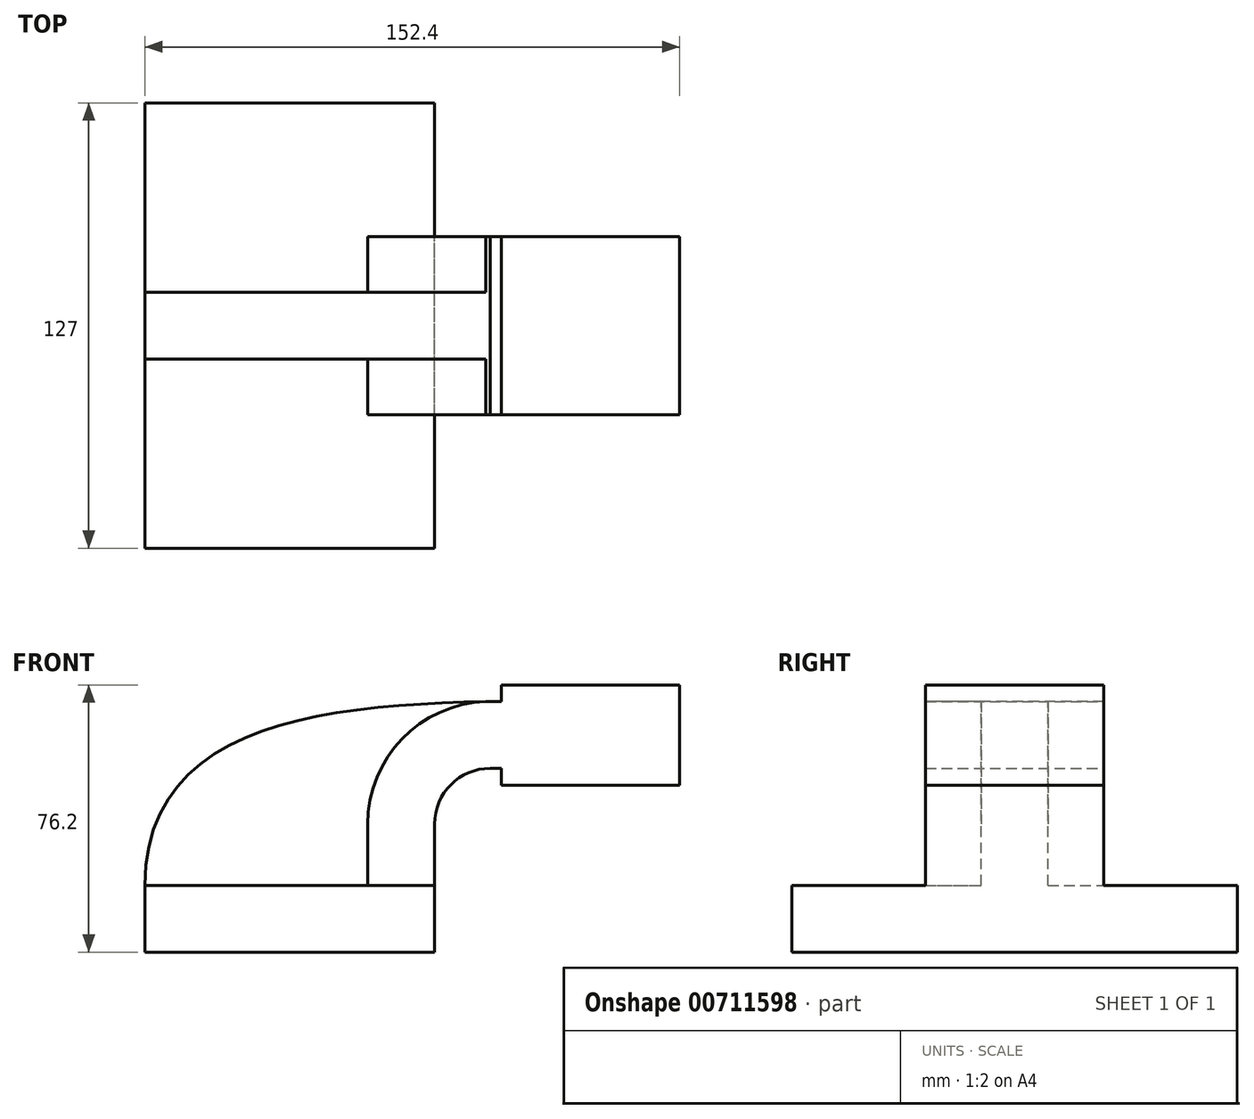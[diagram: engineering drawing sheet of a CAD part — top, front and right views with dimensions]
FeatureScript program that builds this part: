
annotation { "Feature Type Name" : "Feature", "Feature Type Description" : "" }
export const myFeature = defineFeature(function(context is Context, id is Id, definition is map)
    precondition{}
    {
        {
            var Q0;
            Q0=qCreatedBy(makeId("Front.planeOp"),FACE);
            var sketch = newSketch(context, id + "F0", { "sketchPlane" : qUnion([Q0])});
            skLineSegment(sketch, "E0.bottom", {"start": v(41.28, -9.52) * mm, "end": v(-41.28, -9.53) * mm});
            skLineSegment(sketch, "E0.top", {"start": v(41.28, 9.53) * mm, "end": v(-41.28, 9.53) * mm});
            skLineSegment(sketch, "E0.left", {"start": v(41.28, -9.52) * mm, "end": v(41.28, 9.53) * mm});
            skLineSegment(sketch, "E0.right", {"start": v(-41.28, -9.53) * mm, "end": v(-41.28, 9.53) * mm});
            skPoint(sketch, "E0.middle", {"position": v(0, 0) * mm});
            skLineSegment(sketch, "E1.bottom", {"start": v(60.33, 66.68) * mm, "end": v(111.13, 66.68) * mm});
            skLineSegment(sketch, "E1.top", {"start": v(60.33, 38.1) * mm, "end": v(111.13, 38.1) * mm});
            skLineSegment(sketch, "E1.left", {"start": v(60.33, 66.68) * mm, "end": v(60.33, 38.1) * mm});
            skLineSegment(sketch, "E1.right", {"start": v(111.13, 66.68) * mm, "end": v(111.13, 38.1) * mm});
            skPoint(sketch, "E1.middle", {"position": v(85.72, 52.39) * mm});
            skLineSegment(sketch, "E2", {"start": v(41.28, 9.53) * mm, "end": v(41.28, 27) * mm});
            skArc(sketch, "E3", {"start": v(41.27, 27) * mm, "mid": v(45.92, 38.23) * mm, "end": v(57.15, 42.88) * mm});
            skLineSegment(sketch, "E4", {"start": v(57.15, 42.88) * mm, "end": v(85.73, 42.88) * mm});
            skLineSegment(sketch, "E5.0", {"start": v(57.15, 61.93) * mm, "end": v(85.73, 61.93) * mm});
            skArc(sketch, "E5.1", {"start": v(22.23, 27) * mm, "mid": v(32.45, 51.7) * mm, "end": v(57.15, 61.93) * mm});
            skLineSegment(sketch, "E5.2", {"start": v(22.23, 9.53) * mm, "end": v(22.23, 27) * mm});
            skFitSpline(sketch, "E6", {"points": [v(-41.28, 9.53) * mm, v(57.15, 61.93) * mm], "startDerivative": vector(0.26, 138.07) * mm, "endDerivative": vector(143.87, 2.5) * mm});
            skSolve(sketch);
        }
        {
            var Q0;
            Q0=makeQuery(id+"F0.imprint","IMPRINT",FACE,{"disambiguationData":[TD([[makeQuery(id+"F0.imprint","IMPRINT",EDGE,{"derivedFrom":sQuery(id+"F0.wireOp",EDGE,"E0.bottom")}),-1.0]])]});
            extrude(context, id + "F1", {"entities" : qUnion([Q0]), "endBound" : BoundingType.SYMMETRIC, "depth" : 127 * mm, "offsetDistance" : 25.4 * mm});
        }
        {
            var Q0;
            {var subQ1=sQuery(id+"F0.wireOp",EDGE,"E2");Q0=makeQuery(id+"F0.imprint","IMPRINT",FACE,{"disambiguationData":[TD([[makeQuery(id+"F0.imprint","IMPRINT",EDGE,{"derivedFrom":subQ1}),1.0]])]});}
            var Q1;
            {var subQ3=sQuery(id+"F0.wireOp",EDGE,"E1.bottom");Q1=makeQuery(id+"F0.imprint","IMPRINT",FACE,{"disambiguationData":[TD([[makeQuery(id+"F0.imprint","IMPRINT",EDGE,{"derivedFrom":subQ3}),-1.0]])]});}
            extrude(context, id + "F2", {"entities" : qUnion([Q0, Q1]), "operationType" : NewBodyOperationType.ADD, "endBound" : BoundingType.SYMMETRIC, "depth" : 50.8 * mm, "offsetDistance" : 25.4 * mm});
        }
        {
            var Q0;
            {var subQ3=sQuery(id+"F0.wireOp",EDGE,"E5.2");Q0=makeQuery(id+"F0.imprint","IMPRINT",FACE,{"disambiguationData":[TD([[makeQuery(id+"F0.imprint","IMPRINT",EDGE,{"derivedFrom":subQ3}),1.0]])]});}
            extrude(context, id + "F3", {"entities" : qUnion([Q0]), "operationType" : NewBodyOperationType.ADD, "endBound" : BoundingType.SYMMETRIC, "depth" : 19.05 * mm, "offsetDistance" : 25.4 * mm});
        }
    });
